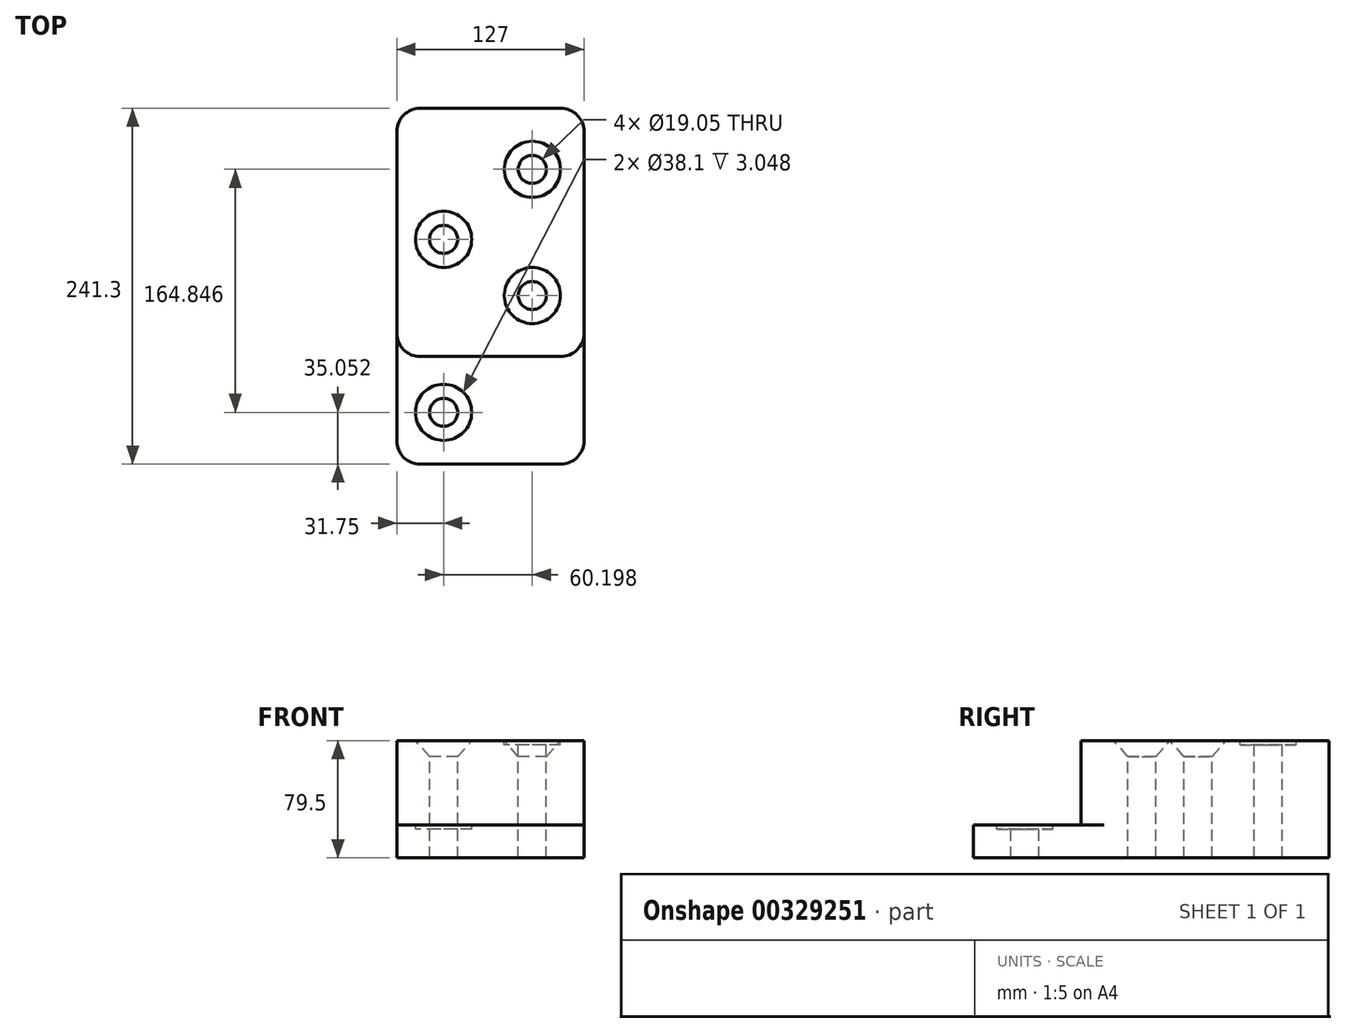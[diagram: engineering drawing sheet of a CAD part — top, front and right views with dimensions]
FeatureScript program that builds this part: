
annotation { "Feature Type Name" : "Feature", "Feature Type Description" : "" }
export const myFeature = defineFeature(function(context is Context, id is Id, definition is map)
    precondition{}
    {
        {
            var Q0;
            Q0=qCreatedBy(makeId("Top.planeOp"),FACE);
            var sketch = newSketch(context, id + "F0", { "sketchPlane" : qUnion([Q0])});
            skLineSegment(sketch, "E0.bottom", {"start": v(0, 0) * mm, "end": v(127, 0) * mm});
            skLineSegment(sketch, "E0.top", {"start": v(0, 241.3) * mm, "end": v(127, 241.3) * mm});
            skLineSegment(sketch, "E0.left", {"start": v(0, 0) * mm, "end": v(0, 241.3) * mm});
            skLineSegment(sketch, "E0.right", {"start": v(127, 0) * mm, "end": v(127, 241.3) * mm});
            skSolve(sketch);
        }
        {
            var Q0;
            Q0=makeQuery(id+"F0.imprint","IMPRINT",FACE,{"disambiguationData":[TD([[makeQuery(id+"F0.imprint","IMPRINT",EDGE,{"derivedFrom":sQuery(id+"F0.wireOp",EDGE,"E0.bottom")}),1.0]])]});
            extrude(context, id + "F1", {"entities" : qUnion([Q0]), "oppositeDirection" : true, "depth" : 22.35 * mm});
        }
        {
            var Q0;
            Q0=qCreatedBy(makeId("Top.planeOp"),FACE);
            var sketch = newSketch(context, id + "F2", { "sketchPlane" : qUnion([Q0])});
            skLineSegment(sketch, "E1.bottom", {"start": v(0, 241.3) * mm, "end": v(127, 241.3) * mm});
            skLineSegment(sketch, "E1.top", {"start": v(0, 72.9) * mm, "end": v(127, 72.9) * mm});
            skLineSegment(sketch, "E1.left", {"start": v(0, 241.3) * mm, "end": v(0, 72.9) * mm});
            skLineSegment(sketch, "E1.right", {"start": v(127, 241.3) * mm, "end": v(127, 72.9) * mm});
            skSolve(sketch);
        }
        {
            var Q0;
            Q0 = qSketchRegion(id + "F2", true);
            extrude(context, id + "F3", {"entities" : qUnion([Q0]), "operationType" : NewBodyOperationType.ADD, "depth" : 57.15 * mm});
        }
        {
            var Q0;
            Q0=makeQuery(id+"F3.opExtrude","SWEPT_EDGE",EDGE,{"disambiguationData":[OSD([sQuery(id+"F2.wireOp",EDGE,"E1.top"),sQuery(id+"F2.wireOp",EDGE,"E1.left")])]});
            var Q1;
            Q1=makeQuery(id+"F3.opExtrude","SWEPT_EDGE",EDGE,{"disambiguationData":[OSD([sQuery(id+"F2.wireOp",EDGE,"E1.top"),sQuery(id+"F2.wireOp",EDGE,"E1.right")])]});
            var Q2;
            Q2=makeQuery(id+"F1.opExtrude","SWEPT_EDGE",EDGE,{"disambiguationData":[OSD([sQuery(id+"F0.wireOp",EDGE,"E0.bottom"),sQuery(id+"F0.wireOp",EDGE,"E0.left")])]});
            var Q3;
            Q3=makeQuery(id+"F1.opExtrude","SWEPT_EDGE",EDGE,{"disambiguationData":[OSD([sQuery(id+"F0.wireOp",EDGE,"E0.bottom"),sQuery(id+"F0.wireOp",EDGE,"E0.right")])]});
            var Q4;
            Q4=makeQuery(id+"F3.boolean.opBoolean","MERGE",EDGE,{"derivedFrom":[makeQuery(id+"F1.opExtrude","SWEPT_EDGE",EDGE,{"disambiguationData":[OSD([sQuery(id+"F0.wireOp",EDGE,"E0.top"),sQuery(id+"F0.wireOp",EDGE,"E0.right")])]}),makeQuery(id+"F3.opExtrude","SWEPT_EDGE",EDGE,{"disambiguationData":[OSD([sQuery(id+"F2.wireOp",EDGE,"E1.bottom"),sQuery(id+"F2.wireOp",EDGE,"E1.right")])]})]});
            var Q5;
            Q5=makeQuery(id+"F3.boolean.opBoolean","MERGE",EDGE,{"derivedFrom":[makeQuery(id+"F1.opExtrude","SWEPT_EDGE",EDGE,{"disambiguationData":[OSD([sQuery(id+"F0.wireOp",EDGE,"E0.top"),sQuery(id+"F0.wireOp",EDGE,"E0.left")])]}),makeQuery(id+"F3.opExtrude","SWEPT_EDGE",EDGE,{"disambiguationData":[OSD([sQuery(id+"F2.wireOp",EDGE,"E1.bottom"),sQuery(id+"F2.wireOp",EDGE,"E1.left")])]})]});
            fillet(context, id + "F4", {"entities" : qUnion([Q0, Q1, Q2, Q3, Q4, Q5]), "radius" : 15.75 * mm, "tangentPropagation" : true, "allowEdgeOverflow" : false});
        }
        {
            var Q0;
            Q0=makeQuery(id+"F3.opExtrude","CAP_FACE",FACE,{"disambiguationData":[OSD([sQuery(id+"F2.wireOp",EDGE,"E1.bottom"),sQuery(id+"F2.wireOp",EDGE,"E1.top"),sQuery(id+"F2.wireOp",EDGE,"E1.left"),sQuery(id+"F2.wireOp",EDGE,"E1.right")])],"isStart":false});
            cPlane(context, id + "F5", {"entities" : qUnion([Q0]), "cplaneType" : CPlaneType.OFFSET, "offset" : 0 * mm, "width" : 152.4 * mm, "height" : 152.4 * mm});
        }
        {
            var Q0;
            Q0=qCreatedBy(id+"F5.planeOp",FACE);
            var sketch = newSketch(context, id + "F6", { "sketchPlane" : qUnion([Q0])});
            skCircle(sketch, "E2", {"center": v(91.95, 199.9) * mm, "radius": 9.53 * mm});
            skCircle(sketch, "E3", {"center": v(31.75, 35.05) * mm, "radius": 9.53 * mm});
            skCircle(sketch, "E4", {"center": v(31.75, 152.4) * mm, "radius": 9.53 * mm});
            skCircle(sketch, "E5", {"center": v(91.95, 114.3) * mm, "radius": 9.53 * mm});
            skSolve(sketch);
        }
        {
            var Q0;
            Q0=makeQuery(id+"F6.imprint","IMPRINT",FACE,{"disambiguationData":[TD([[makeQuery(id+"F6.imprint","IMPRINT",EDGE,{"derivedFrom":sQuery(id+"F6.wireOp",EDGE,"E2")}),1.0]])]});
            var Q1;
            Q1=makeQuery(id+"F6.imprint","IMPRINT",FACE,{"disambiguationData":[TD([[makeQuery(id+"F6.imprint","IMPRINT",EDGE,{"derivedFrom":sQuery(id+"F6.wireOp",EDGE,"E3")}),1.0]])]});
            var Q2;
            Q2=makeQuery(id+"F6.imprint","IMPRINT",FACE,{"disambiguationData":[TD([[makeQuery(id+"F6.imprint","IMPRINT",EDGE,{"derivedFrom":sQuery(id+"F6.wireOp",EDGE,"E4")}),1.0]])]});
            var Q3;
            Q3=makeQuery(id+"F6.imprint","IMPRINT",FACE,{"disambiguationData":[TD([[makeQuery(id+"F6.imprint","IMPRINT",EDGE,{"derivedFrom":sQuery(id+"F6.wireOp",EDGE,"E5")}),1.0]])]});
            extrude(context, id + "F7", {"entities" : qUnion([Q0, Q1, Q2, Q3]), "operationType" : NewBodyOperationType.REMOVE, "endBound" : BoundingType.THROUGH_ALL, "oppositeDirection" : true, "depth" : 25.4 * mm});
        }
        {
            var Q0;
            Q0=qCreatedBy(id+"F5.planeOp",FACE);
            var sketch = newSketch(context, id + "F8", { "sketchPlane" : qUnion([Q0])});
            skCircle(sketch, "E6", {"center": v(91.95, 199.9) * mm, "radius": 19.05 * mm});
            skSolve(sketch);
        }
        {
            var Q0;
            Q0=makeQuery(id+"F8.imprint","IMPRINT",FACE,{"disambiguationData":[TD([[makeQuery(id+"F8.imprint","IMPRINT",EDGE,{"derivedFrom":sQuery(id+"F8.wireOp",EDGE,"E6")}),1.0]])]});
            extrude(context, id + "F9", {"entities" : qUnion([Q0]), "operationType" : NewBodyOperationType.REMOVE, "oppositeDirection" : true, "depth" : 3.05 * mm});
        }
        {
            var Q0;
            Q0=makeQuery(id+"F1.opExtrude","CAP_FACE",FACE,{"disambiguationData":[OSD([sQuery(id+"F0.wireOp",EDGE,"E0.bottom"),sQuery(id+"F0.wireOp",EDGE,"E0.top"),sQuery(id+"F0.wireOp",EDGE,"E0.left"),sQuery(id+"F0.wireOp",EDGE,"E0.right")])],"isStart":true});
            cPlane(context, id + "F10", {"entities" : qUnion([Q0]), "cplaneType" : CPlaneType.OFFSET, "offset" : 0 * mm, "width" : 152.4 * mm, "height" : 152.4 * mm});
        }
        {
            var Q0;
            Q0=qCreatedBy(id+"F10.planeOp",FACE);
            var sketch = newSketch(context, id + "F11", { "sketchPlane" : qUnion([Q0])});
            skCircle(sketch, "E7", {"center": v(31.75, 35.05) * mm, "radius": 19.05 * mm});
            skSolve(sketch);
        }
        {
            var Q0;
            Q0=makeQuery(id+"F11.imprint","IMPRINT",FACE,{"disambiguationData":[TD([[makeQuery(id+"F11.imprint","IMPRINT",EDGE,{"derivedFrom":sQuery(id+"F11.wireOp",EDGE,"E7")}),1.0]])]});
            extrude(context, id + "F12", {"entities" : qUnion([Q0]), "operationType" : NewBodyOperationType.REMOVE, "oppositeDirection" : true, "depth" : 3.05 * mm});
        }
        {
            var Q0;
            Q0=sQuery(id+"F6.wireOp",VERTEX,"E4.center");
            var Q1;
            Q1=sQuery(id+"F6.wireOp",VERTEX,"E5.center");
            var Q2;
            Q2=makeQuery(id+"F1.opExtrude","SWEPT_BODY",BODY,{"disambiguationData":[OSD([sQuery(id+"F0.wireOp",EDGE,"E0.bottom"),sQuery(id+"F0.wireOp",EDGE,"E0.top"),sQuery(id+"F0.wireOp",EDGE,"E0.left"),sQuery(id+"F0.wireOp",EDGE,"E0.right")])]});
            hole(context, id + "F13", {"style" : HoleStyle.C_SINK, "endStyle" : HoleEndStyle.THROUGH, "holeDiameter" : 19.05 * mm, "cSinkDiameter" : 38.1 * mm, "cSinkAngle" : 82 * degree, "tappedDepth" : 12.7 * mm, "tapClearance" : 3, "startFromSketch" : true, "locations" : qUnion([Q0, Q1]), "scope" : qUnion([Q2])});
        }
    });
